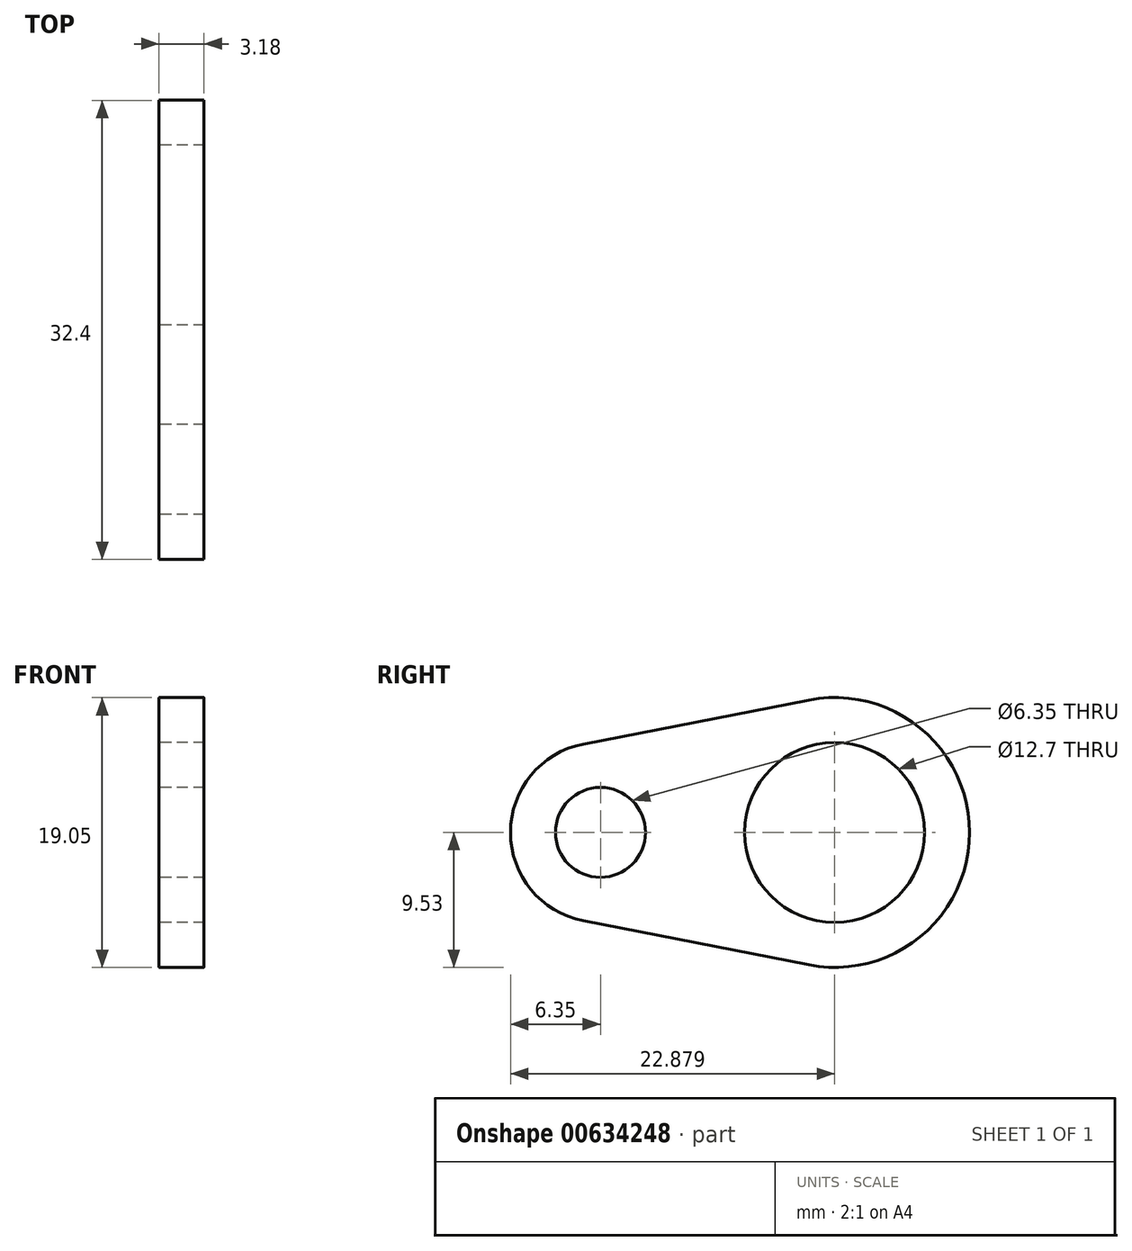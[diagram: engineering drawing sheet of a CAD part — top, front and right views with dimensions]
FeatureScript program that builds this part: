
annotation { "Feature Type Name" : "Feature", "Feature Type Description" : "" }
export const myFeature = defineFeature(function(context is Context, id is Id, definition is map)
    precondition{}
    {
        {
            var Q0;
            Q0=qCreatedBy(makeId("Right.planeOp"),FACE);
            var sketch = newSketch(context, id + "F0", { "sketchPlane" : qUnion([Q0])});
            skCircle(sketch, "E0", {"center": v(0, 0) * mm, "radius": 3.18 * mm});
            skCircle(sketch, "E1", {"center": v(16.53, 0) * mm, "radius": 6.35 * mm});
            skCircle(sketch, "E2.0", {"center": v(16.53, 0) * mm, "radius": 9.53 * mm, "construction": true});
            skCircle(sketch, "E3.0", {"center": v(0, 0) * mm, "radius": 6.35 * mm, "construction": true});
            skLineSegment(sketch, "E4", {"start": v(-1.22, 6.23) * mm, "end": v(14.7, 9.35) * mm});
            skLineSegment(sketch, "E5", {"start": v(-1.22, -6.23) * mm, "end": v(14.7, -9.35) * mm});
            skArc(sketch, "E6", {"start": v(14.7, 9.35) * mm, "mid": v(26.05, 0) * mm, "end": v(14.7, -9.35) * mm});
            skArc(sketch, "E7", {"start": v(-1.22, 6.23) * mm, "mid": v(-6.35, 0) * mm, "end": v(-1.22, -6.23) * mm});
            skSolve(sketch);
        }
        {
            var Q0;
            Q0=qSketchRegion(id+"F0",true);
            extrude(context, id + "F1", {"entities" : qUnion([Q0]), "depth" : 3.17 * mm, "offsetDistance" : 25.4 * mm});
        }
    });
